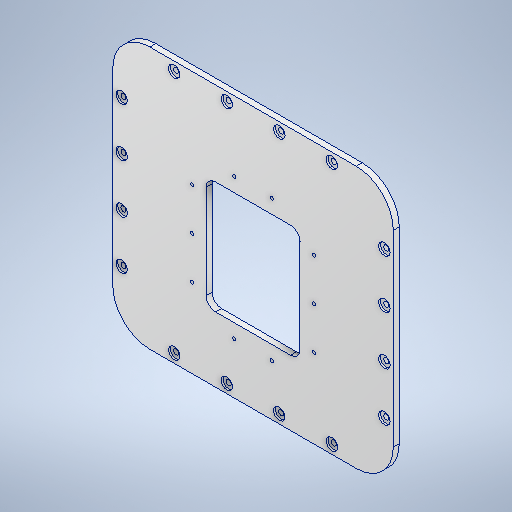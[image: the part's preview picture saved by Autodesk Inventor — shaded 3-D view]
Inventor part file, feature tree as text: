
AUTODESK INVENTOR PART (.ipt)
format: ipt  version: 2025.2 (Build 292293000, 293)  size: 359,936 bytes
history: native  units: in
note: dims shown in document units (in); Inventor stores cm internally (conversion verified against a paired STEP export)
features: hole x2, sketch x2, other x2, plane x1, extrude x1, reference x1
ambient origin geometry x8: Origin, YZ Plane, XZ Plane, XY Plane, X Axis, Y Axis, Z Axis, Center Point
bodies: Solid1 (feature_tree)
feature tree (9):
  plane  "Work Plane2"
  extrude  "Extrusion1"  Depth=4.7244in
  hole  "Hole1"  [1 undecoded]
  hole  "Hole2"  [1 undecoded]
  sketch  "Sketch1"  dims[d1=3.937in d2=4.7244in]
  reference  "Reference10"
  sketch  "Sketch3"  dims[d3=0.3937in d4=0.25in d5=0.0in d7=0.2165in d8=0.315in d9=0.4819in d10=0.0787in d11=90.0deg d12=0.315in d13=0.8108in d18=1.7717in d19=1.7717in d22=1.7717in d23=1.7717in d26=0.1362in d27=0.315in d28=0.3701in d29=0.0787in d30=90.0deg d31=0.4252in d32=0.8108in]
  other  "Assembly1"
  other  "the big cover v1:1"
note: 2 required parameter values undecoded (feature->parameter linkage not recoverable at this tier; creation-order binding heuristic only, values carry confidence <= 0.55)
